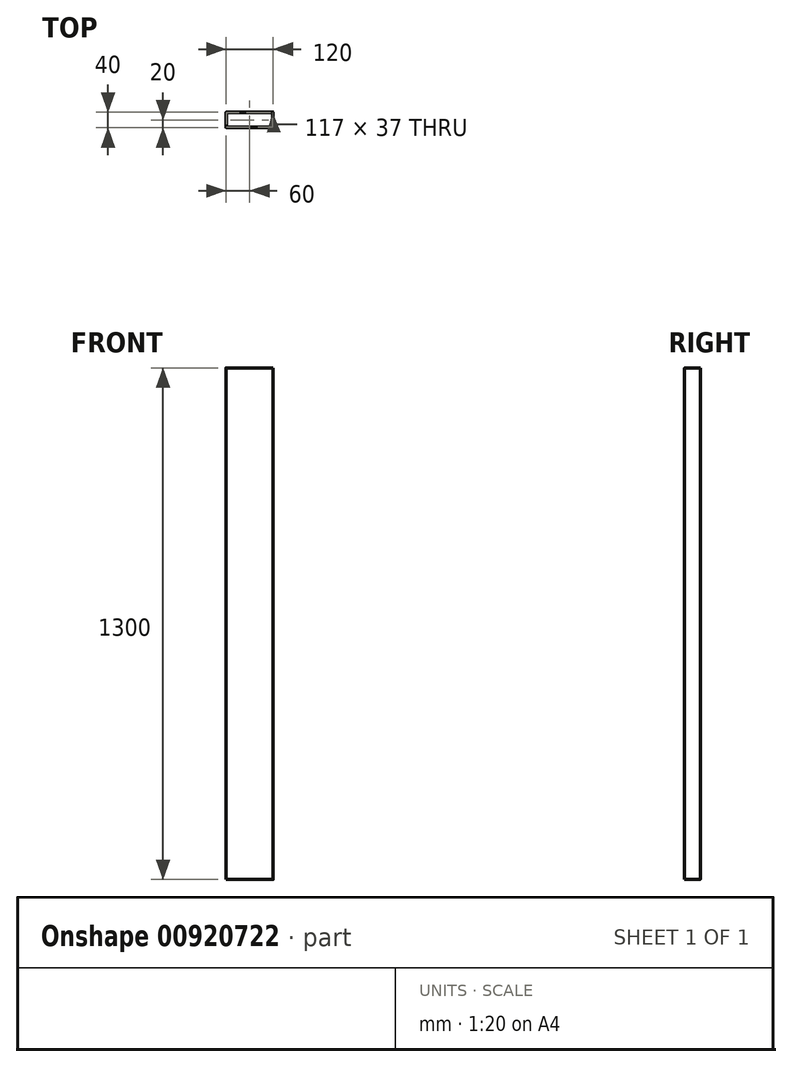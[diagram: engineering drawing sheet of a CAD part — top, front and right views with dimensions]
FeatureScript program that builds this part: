
annotation { "Feature Type Name" : "Feature", "Feature Type Description" : "" }
export const myFeature = defineFeature(function(context is Context, id is Id, definition is map)
    precondition{}
    {
        {
            var Q0;
            Q0=qCreatedBy(makeId("Top.planeOp"),FACE);
            var sketch = newSketch(context, id + "F0", { "sketchPlane" : qUnion([Q0])});
            skLineSegment(sketch, "E0.bottom", {"start": v(59.6, 20) * mm, "end": v(-59.6, 20) * mm});
            skLineSegment(sketch, "E0.top", {"start": v(59.6, -20) * mm, "end": v(-59.6, -20) * mm});
            skLineSegment(sketch, "E0.left", {"start": v(60, 19.6) * mm, "end": v(60, -19.6) * mm});
            skLineSegment(sketch, "E0.right", {"start": v(-60, 19.6) * mm, "end": v(-60, -19.6) * mm});
            skPoint(sketch, "E0.middle", {"position": v(0, 0) * mm});
            skPoint(sketch, "E1.visualSharp", {"position": v(-60, 20) * mm});
            skArc(sketch, "E1.filletArc", {"start": v(-59.6, 20) * mm, "mid": v(-59.88, 19.88) * mm, "end": v(-60, 19.6) * mm});
            skPoint(sketch, "E2.visualSharp", {"position": v(-60, -20) * mm});
            skArc(sketch, "E2.filletArc", {"start": v(-60, -19.6) * mm, "mid": v(-59.88, -19.88) * mm, "end": v(-59.6, -20) * mm});
            skPoint(sketch, "E3.visualSharp", {"position": v(60, -20) * mm});
            skArc(sketch, "E3.filletArc", {"start": v(59.6, -20) * mm, "mid": v(59.88, -19.88) * mm, "end": v(60, -19.6) * mm});
            skPoint(sketch, "E4.visualSharp", {"position": v(60, 20) * mm});
            skArc(sketch, "E4.filletArc", {"start": v(60, 19.6) * mm, "mid": v(59.88, 19.88) * mm, "end": v(59.6, 20) * mm});
            skLineSegment(sketch, "E5.0", {"start": v(58.5, 18.5) * mm, "end": v(58.5, -18.5) * mm});
            skLineSegment(sketch, "E5.1", {"start": v(58.5, 18.5) * mm, "end": v(-58.5, 18.5) * mm});
            skLineSegment(sketch, "E5.2", {"start": v(-58.5, 18.5) * mm, "end": v(-58.5, -18.5) * mm});
            skLineSegment(sketch, "E5.3", {"start": v(58.5, -18.5) * mm, "end": v(-58.5, -18.5) * mm});
            skSolve(sketch);
        }
        {
            var Q0;
            Q0 = qSketchRegion(id + "F0", true);
            extrude(context, id + "F1", {"entities" : qUnion([Q0]), "depth" : 1300 * mm, "offsetDistance" : 25 * mm});
        }
    });
